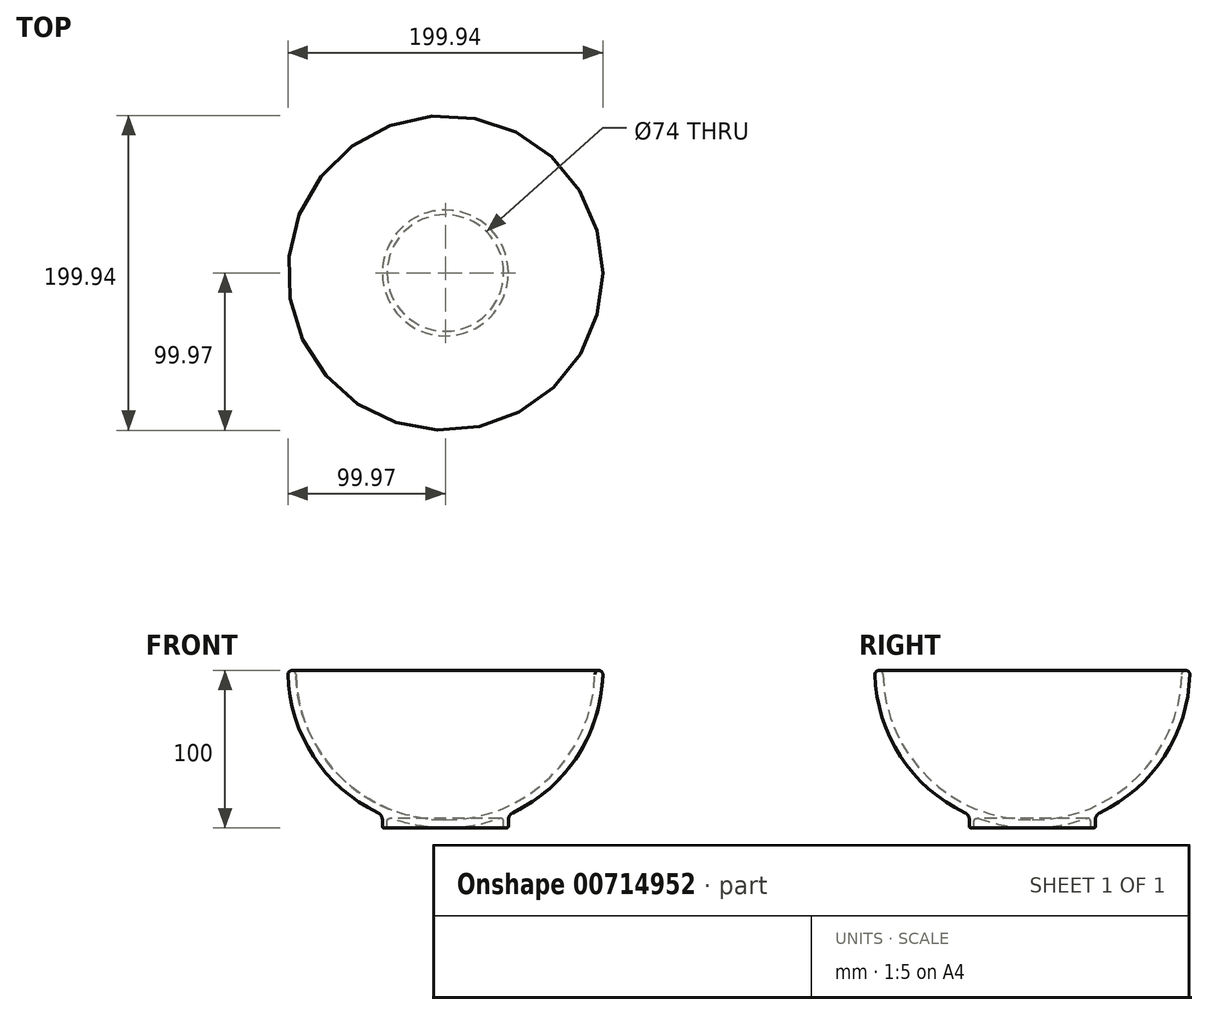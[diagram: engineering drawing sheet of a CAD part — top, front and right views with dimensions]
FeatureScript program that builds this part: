
annotation { "Feature Type Name" : "Feature", "Feature Type Description" : "" }
export const myFeature = defineFeature(function(context is Context, id is Id, definition is map)
    precondition{}
    {
        {
            var Q0;
            Q0=qCreatedBy(makeId("Front.planeOp"),FACE);
            var sketch = newSketch(context, id + "F0", { "sketchPlane" : qUnion([Q0])});
            skArc(sketch, "E0", {"start": v(-100, 100) * mm, "mid": v(-84.52, 46.55) * mm, "end": v(-42.86, 9.65) * mm});
            skArc(sketch, "E1.0", {"start": v(-95, 100) * mm, "mid": v(-67.18, 32.82) * mm, "end": v(0, 5) * mm});
            skLineSegment(sketch, "E2", {"start": v(-38, 0) * mm, "end": v(-39, 0) * mm});
            skLineSegment(sketch, "E3", {"start": v(-40, 1) * mm, "end": v(-40, 5.13) * mm});
            skPoint(sketch, "E4.orphan", {"position": v(100, 100) * mm});
            skLineSegment(sketch, "E5", {"start": v(0, 5) * mm, "end": v(0, 0) * mm});
            skLineSegment(sketch, "E6", {"start": v(-37, 1) * mm, "end": v(-37, 4.2) * mm});
            skArc(sketch, "E7.trimOffspring", {"start": v(-34.31, 6.07) * mm, "mid": v(-17.42, 1.53) * mm, "end": v(0, 0) * mm});
            skPoint(sketch, "E8.visualSharp", {"position": v(-37, 7.1) * mm});
            skArc(sketch, "E8.filletArc", {"start": v(-34.31, 6.07) * mm, "mid": v(-36.15, 5.83) * mm, "end": v(-37, 4.2) * mm});
            skPoint(sketch, "E9.visualSharp", {"position": v(-40, 8.35) * mm});
            skArc(sketch, "E9.filletArc", {"start": v(-40, 5.13) * mm, "mid": v(-40.77, 7.8) * mm, "end": v(-42.86, 9.65) * mm});
            skPoint(sketch, "E10.visualSharp", {"position": v(-40, 0) * mm});
            skArc(sketch, "E10.filletArc", {"start": v(-40, 1) * mm, "mid": v(-39.7, 0.3) * mm, "end": v(-39, 0) * mm});
            skPoint(sketch, "E11.visualSharp", {"position": v(-37, 0) * mm});
            skArc(sketch, "E11.filletArc", {"start": v(-38, 0) * mm, "mid": v(-37.3, 0.3) * mm, "end": v(-37, 1) * mm});
            skLineSegment(sketch, "E12", {"start": v(-100, 100) * mm, "end": v(-95, 100) * mm});
            skSolve(sketch);
        }
        {
            var Q0;
            Q0=makeQuery(id+"F0.imprint","IMPRINT",FACE,{"disambiguationData":[TD([[makeQuery(id+"F0.imprint","IMPRINT",EDGE,{"derivedFrom":sQuery(id+"F0.wireOp",EDGE,"E0")}),1.0]])]});
            var Q1;
            Q1=sQuery(id+"F0.wireOp",EDGE,"E5");
            revolve(context, id + "F1", {"surfaceOperationType" : NewSurfaceOperationType.NEW, "entities" : qUnion([Q0]), "axis" : qUnion([Q1]), "revolveType" : RevolveType.FULL});
        }
        {
            var Q0;
            Q0=makeQuery(id+"F1.opRevolve","SWEPT_EDGE",EDGE,{"disambiguationData":[OSD([sQuery(id+"F0.wireOp",EDGE,"E0"),sQuery(id+"F0.wireOp",EDGE,"E12")])]});
            var Q1;
            Q1=makeQuery(id+"F1.opRevolve","SWEPT_EDGE",EDGE,{"disambiguationData":[OSD([sQuery(id+"F0.wireOp",EDGE,"E1.0"),sQuery(id+"F0.wireOp",EDGE,"E12")])]});
            fillet(context, id + "F2", {"entities" : qUnion([Q0, Q1]), "radius" : 2.5 * mm, "tangentPropagation" : true, "allowEdgeOverflow" : false});
        }
    });
